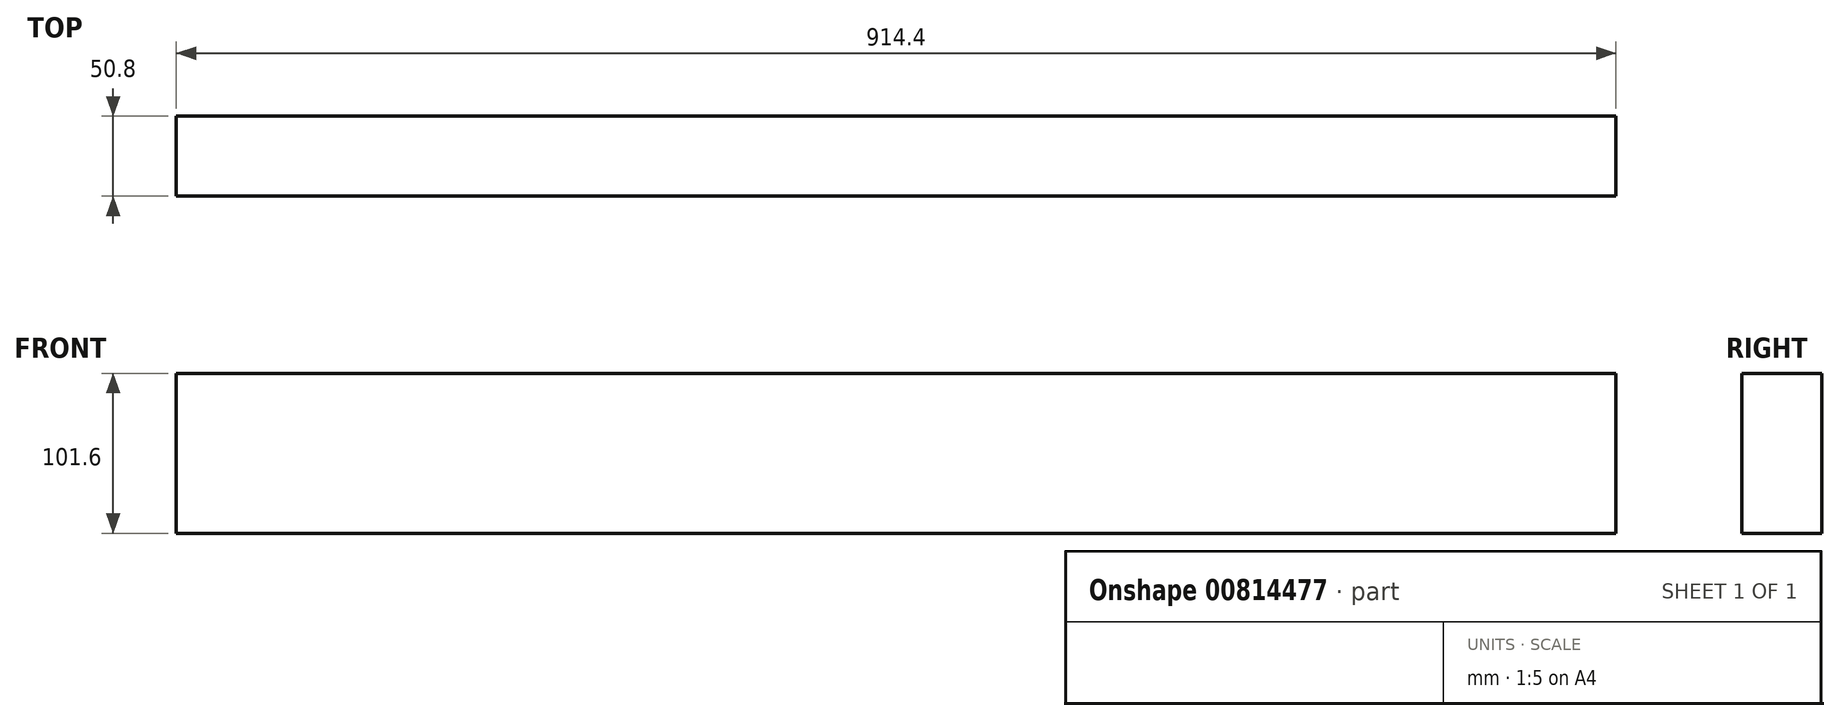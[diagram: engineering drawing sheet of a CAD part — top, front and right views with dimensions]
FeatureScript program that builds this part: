
annotation { "Feature Type Name" : "Feature", "Feature Type Description" : "" }
export const myFeature = defineFeature(function(context is Context, id is Id, definition is map)
    precondition{}
    {
        {
            var Q0;
            Q0=qCreatedBy(makeId("Front.planeOp"),FACE);
            var sketch = newSketch(context, id + "F0", { "sketchPlane" : qUnion([Q0])});
            skLineSegment(sketch, "E0.bottom", {"start": v(0, 0) * mm, "end": v(914.4, 0) * mm});
            skLineSegment(sketch, "E0.top", {"start": v(0, 101.6) * mm, "end": v(914.4, 101.6) * mm});
            skLineSegment(sketch, "E0.left", {"start": v(0, 0) * mm, "end": v(0, 101.6) * mm});
            skLineSegment(sketch, "E0.right", {"start": v(914.4, 0) * mm, "end": v(914.4, 101.6) * mm});
            skSolve(sketch);
        }
        {
            var Q0;
            Q0 = qSketchRegion(id + "F0", true);
            extrude(context, id + "F1", {"entities" : qUnion([Q0]), "depth" : 50.8 * mm, "offsetDistance" : 25.4 * mm});
        }
    });
